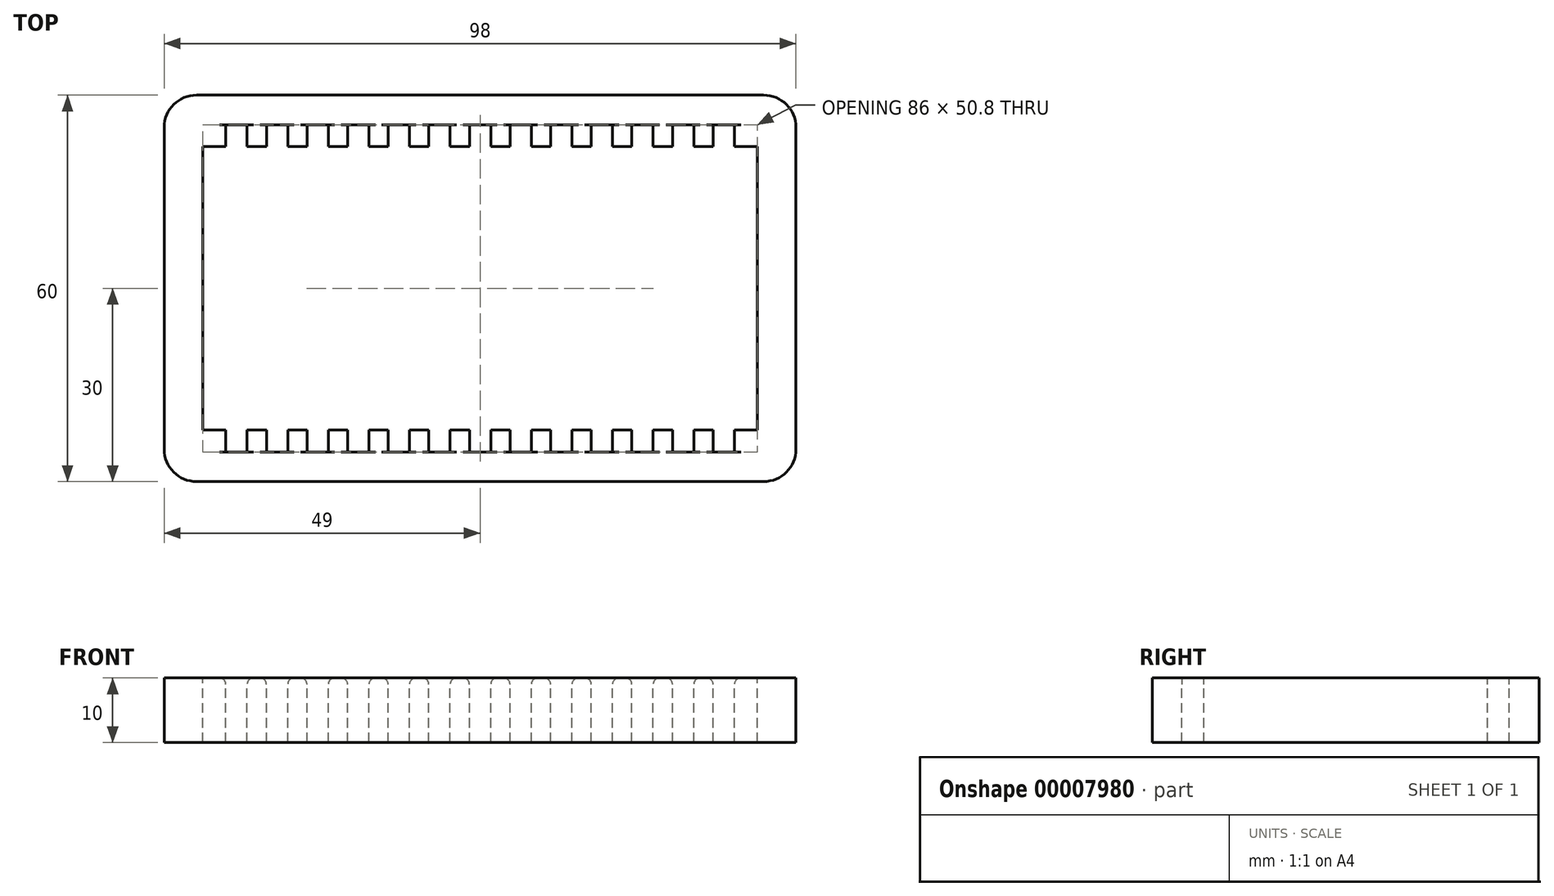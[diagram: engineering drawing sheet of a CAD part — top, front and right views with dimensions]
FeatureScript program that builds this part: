
annotation { "Feature Type Name" : "Feature", "Feature Type Description" : "" }
export const myFeature = defineFeature(function(context is Context, id is Id, definition is map)
    precondition{}
    {
        {
            var Q0;
            Q0=qCreatedBy(makeId("Top.planeOp"),FACE);
            var sketch = newSketch(context, id + "F0", { "sketchPlane" : qUnion([Q0])});
            skLineSegment(sketch, "E0.bottom", {"start": v(46, 3) * mm, "end": v(-46, 3) * mm});
            skLineSegment(sketch, "E0.top", {"start": v(49, -3) * mm, "end": v(-49, -3) * mm});
            skLineSegment(sketch, "E0.left", {"start": v(49, 0) * mm, "end": v(49, -3) * mm});
            skLineSegment(sketch, "E0.right", {"start": v(-49, 0) * mm, "end": v(-49, -3) * mm});
            skPoint(sketch, "E0.middle", {"position": v(0, 0) * mm});
            skLineSegment(sketch, "E1.bottom", {"start": v(-45.75, -3) * mm, "end": v(-42.45, -3) * mm});
            skLineSegment(sketch, "E1.top", {"start": v(-45.75, 0) * mm, "end": v(-42.45, 0) * mm});
            skLineSegment(sketch, "E1.left", {"start": v(-45.75, -3) * mm, "end": v(-45.75, 0) * mm});
            skLineSegment(sketch, "E1.right", {"start": v(-42.45, -3) * mm, "end": v(-42.45, 0) * mm});
            skLineSegment(sketch, "E2.1.0.0", {"start": v(-36.15, -3) * mm, "end": v(-36.15, 0) * mm});
            skLineSegment(sketch, "E2.1.0.1", {"start": v(-39.45, 0) * mm, "end": v(-36.15, 0) * mm});
            skLineSegment(sketch, "E2.1.0.2", {"start": v(-39.45, -3) * mm, "end": v(-39.45, 0) * mm});
            skLineSegment(sketch, "E2.2.0.0", {"start": v(-29.85, -3) * mm, "end": v(-29.85, 0) * mm});
            skLineSegment(sketch, "E2.2.0.1", {"start": v(-33.15, 0) * mm, "end": v(-29.85, 0) * mm});
            skLineSegment(sketch, "E2.2.0.2", {"start": v(-33.15, -3) * mm, "end": v(-33.15, 0) * mm});
            skLineSegment(sketch, "E2.3.0.0", {"start": v(-23.55, -3) * mm, "end": v(-23.55, 0) * mm});
            skLineSegment(sketch, "E2.3.0.1", {"start": v(-26.85, 0) * mm, "end": v(-23.55, 0) * mm});
            skLineSegment(sketch, "E2.3.0.2", {"start": v(-26.85, -3) * mm, "end": v(-26.85, 0) * mm});
            skLineSegment(sketch, "E2.4.0.0", {"start": v(-17.25, -3) * mm, "end": v(-17.25, 0) * mm});
            skLineSegment(sketch, "E2.4.0.1", {"start": v(-20.55, 0) * mm, "end": v(-17.25, 0) * mm});
            skLineSegment(sketch, "E2.4.0.2", {"start": v(-20.55, -3) * mm, "end": v(-20.55, 0) * mm});
            skLineSegment(sketch, "E2.5.0.0", {"start": v(-10.95, -3) * mm, "end": v(-10.95, 0) * mm});
            skLineSegment(sketch, "E2.5.0.1", {"start": v(-14.25, 0) * mm, "end": v(-10.95, 0) * mm});
            skLineSegment(sketch, "E2.5.0.2", {"start": v(-14.25, -3) * mm, "end": v(-14.25, 0) * mm});
            skLineSegment(sketch, "E2.6.0.0", {"start": v(-4.65, -3) * mm, "end": v(-4.65, 0) * mm});
            skLineSegment(sketch, "E2.6.0.1", {"start": v(-7.95, 0) * mm, "end": v(-4.65, 0) * mm});
            skLineSegment(sketch, "E2.6.0.2", {"start": v(-7.95, -3) * mm, "end": v(-7.95, 0) * mm});
            skLineSegment(sketch, "E2.7.0.0", {"start": v(1.65, -3) * mm, "end": v(1.65, 0) * mm});
            skLineSegment(sketch, "E2.7.0.1", {"start": v(-1.65, 0) * mm, "end": v(1.65, 0) * mm});
            skLineSegment(sketch, "E2.7.0.2", {"start": v(-1.65, -3) * mm, "end": v(-1.65, 0) * mm});
            skLineSegment(sketch, "E2.8.0.0", {"start": v(7.95, -3) * mm, "end": v(7.95, 0) * mm});
            skLineSegment(sketch, "E2.8.0.1", {"start": v(4.65, 0) * mm, "end": v(7.95, 0) * mm});
            skLineSegment(sketch, "E2.8.0.2", {"start": v(4.65, -3) * mm, "end": v(4.65, 0) * mm});
            skLineSegment(sketch, "E2.9.0.0", {"start": v(14.25, -3) * mm, "end": v(14.25, 0) * mm});
            skLineSegment(sketch, "E2.9.0.1", {"start": v(10.95, 0) * mm, "end": v(14.25, 0) * mm});
            skLineSegment(sketch, "E2.9.0.2", {"start": v(10.95, -3) * mm, "end": v(10.95, 0) * mm});
            skLineSegment(sketch, "E2.10.0.0", {"start": v(20.55, -3) * mm, "end": v(20.55, 0) * mm});
            skLineSegment(sketch, "E2.10.0.1", {"start": v(17.25, 0) * mm, "end": v(20.55, 0) * mm});
            skLineSegment(sketch, "E2.10.0.2", {"start": v(17.25, -3) * mm, "end": v(17.25, 0) * mm});
            skLineSegment(sketch, "E2.11.0.0", {"start": v(26.85, -3) * mm, "end": v(26.85, 0) * mm});
            skLineSegment(sketch, "E2.11.0.1", {"start": v(23.55, 0) * mm, "end": v(26.85, 0) * mm});
            skLineSegment(sketch, "E2.11.0.2", {"start": v(23.55, -3) * mm, "end": v(23.55, 0) * mm});
            skLineSegment(sketch, "E2.12.0.0", {"start": v(33.15, -3) * mm, "end": v(33.15, 0) * mm});
            skLineSegment(sketch, "E2.12.0.1", {"start": v(29.85, 0) * mm, "end": v(33.15, 0) * mm});
            skLineSegment(sketch, "E2.12.0.2", {"start": v(29.85, -3) * mm, "end": v(29.85, 0) * mm});
            skLineSegment(sketch, "E2.13.0.0", {"start": v(39.45, -3) * mm, "end": v(39.45, 0) * mm});
            skLineSegment(sketch, "E2.13.0.1", {"start": v(36.15, 0) * mm, "end": v(39.45, 0) * mm});
            skLineSegment(sketch, "E2.13.0.2", {"start": v(36.15, -3) * mm, "end": v(36.15, 0) * mm});
            skLineSegment(sketch, "E2.14.0.0", {"start": v(45.75, -3) * mm, "end": v(45.75, 0) * mm});
            skLineSegment(sketch, "E2.14.0.1", {"start": v(42.45, 0) * mm, "end": v(45.75, 0) * mm});
            skLineSegment(sketch, "E2.14.0.2", {"start": v(42.45, -3) * mm, "end": v(42.45, 0) * mm});
            skLineSegment(sketch, "E2.direction1", {"start": v(-42.45, -3) * mm, "end": v(-36.15, -3) * mm, "construction": true});
            skPoint(sketch, "E3.visualSharp", {"position": v(-49, 3) * mm});
            skArc(sketch, "E3.filletArc", {"start": v(-46, 3) * mm, "mid": v(-48.12, 2.12) * mm, "end": v(-49, 0) * mm});
            skPoint(sketch, "E4.visualSharp", {"position": v(49, 3) * mm});
            skArc(sketch, "E4.filletArc", {"start": v(49, 0) * mm, "mid": v(48.12, 2.12) * mm, "end": v(46, 3) * mm});
            skSolve(sketch);
        }
        {
            var Q0;
            Q0=qCreatedBy(makeId("Top.planeOp"),FACE);
            var sketch = newSketch(context, id + "F1", { "sketchPlane" : qUnion([Q0])});
            skLineSegment(sketch, "E5.bottom", {"start": v(44, -30) * mm, "end": v(-44, -30) * mm});
            skLineSegment(sketch, "E5.top", {"start": v(44, 30) * mm, "end": v(-44, 30) * mm});
            skLineSegment(sketch, "E5.left", {"start": v(49, -25) * mm, "end": v(49, 25) * mm});
            skLineSegment(sketch, "E5.right", {"start": v(-49, -25) * mm, "end": v(-49, 25) * mm});
            skPoint(sketch, "E5.middle", {"position": v(0, 0) * mm});
            skLineSegment(sketch, "E6.bottom", {"start": v(43, -22) * mm, "end": v(-43, -22) * mm});
            skLineSegment(sketch, "E6.top", {"start": v(43, 22) * mm, "end": v(-43, 22) * mm});
            skLineSegment(sketch, "E6.left", {"start": v(43, -22) * mm, "end": v(43, 22) * mm});
            skLineSegment(sketch, "E6.right", {"start": v(-43, -22) * mm, "end": v(-43, 22) * mm});
            skPoint(sketch, "E7.visualSharp", {"position": v(-49, 30) * mm});
            skArc(sketch, "E7.filletArc", {"start": v(-44, 30) * mm, "mid": v(-47.54, 28.54) * mm, "end": v(-49, 25) * mm});
            skPoint(sketch, "E8.visualSharp", {"position": v(49, 30) * mm});
            skArc(sketch, "E8.filletArc", {"start": v(49, 25) * mm, "mid": v(47.54, 28.54) * mm, "end": v(44, 30) * mm});
            skPoint(sketch, "E9.visualSharp", {"position": v(49, -30) * mm});
            skArc(sketch, "E9.filletArc", {"start": v(44, -30) * mm, "mid": v(47.54, -28.54) * mm, "end": v(49, -25) * mm});
            skPoint(sketch, "E10.visualSharp", {"position": v(-49, -30) * mm});
            skArc(sketch, "E10.filletArc", {"start": v(-49, -25) * mm, "mid": v(-47.54, -28.54) * mm, "end": v(-44, -30) * mm});
            skLineSegment(sketch, "E11.bottom", {"start": v(-1.65, 25.4) * mm, "end": v(1.65, 25.4) * mm});
            skLineSegment(sketch, "E11.top", {"start": v(-1.65, -25.4) * mm, "end": v(1.65, -25.4) * mm});
            skLineSegment(sketch, "E11.left", {"start": v(-1.65, 25.4) * mm, "end": v(-1.65, -25.4) * mm});
            skLineSegment(sketch, "E11.right", {"start": v(1.65, 25.4) * mm, "end": v(1.65, -25.4) * mm});
            skLineSegment(sketch, "E12", {"start": v(0, 25.4) * mm, "end": v(0, -25.4) * mm, "construction": true});
            skLineSegment(sketch, "E13.1.0.0", {"start": v(4.65, 25.4) * mm, "end": v(7.95, 25.4) * mm});
            skLineSegment(sketch, "E13.1.0.1", {"start": v(4.65, 25.4) * mm, "end": v(4.65, -25.4) * mm});
            skLineSegment(sketch, "E13.1.0.2", {"start": v(7.95, 25.4) * mm, "end": v(7.95, -25.4) * mm});
            skLineSegment(sketch, "E13.1.0.3", {"start": v(4.65, -25.4) * mm, "end": v(7.95, -25.4) * mm});
            skLineSegment(sketch, "E13.2.0.0", {"start": v(10.95, 25.4) * mm, "end": v(14.25, 25.4) * mm});
            skLineSegment(sketch, "E13.2.0.1", {"start": v(10.95, 25.4) * mm, "end": v(10.95, -25.4) * mm});
            skLineSegment(sketch, "E13.2.0.2", {"start": v(14.25, 25.4) * mm, "end": v(14.25, -25.4) * mm});
            skLineSegment(sketch, "E13.2.0.3", {"start": v(10.95, -25.4) * mm, "end": v(14.25, -25.4) * mm});
            skLineSegment(sketch, "E13.3.0.0", {"start": v(17.25, 25.4) * mm, "end": v(20.55, 25.4) * mm});
            skLineSegment(sketch, "E13.3.0.1", {"start": v(17.25, 25.4) * mm, "end": v(17.25, -25.4) * mm});
            skLineSegment(sketch, "E13.3.0.2", {"start": v(20.55, 25.4) * mm, "end": v(20.55, -25.4) * mm});
            skLineSegment(sketch, "E13.3.0.3", {"start": v(17.25, -25.4) * mm, "end": v(20.55, -25.4) * mm});
            skLineSegment(sketch, "E13.4.0.0", {"start": v(23.55, 25.4) * mm, "end": v(26.85, 25.4) * mm});
            skLineSegment(sketch, "E13.4.0.1", {"start": v(23.55, 25.4) * mm, "end": v(23.55, -25.4) * mm});
            skLineSegment(sketch, "E13.4.0.2", {"start": v(26.85, 25.4) * mm, "end": v(26.85, -25.4) * mm});
            skLineSegment(sketch, "E13.4.0.3", {"start": v(23.55, -25.4) * mm, "end": v(26.85, -25.4) * mm});
            skLineSegment(sketch, "E13.5.0.0", {"start": v(29.85, 25.4) * mm, "end": v(33.15, 25.4) * mm});
            skLineSegment(sketch, "E13.5.0.1", {"start": v(29.85, 25.4) * mm, "end": v(29.85, -25.4) * mm});
            skLineSegment(sketch, "E13.5.0.2", {"start": v(33.15, 25.4) * mm, "end": v(33.15, -25.4) * mm});
            skLineSegment(sketch, "E13.5.0.3", {"start": v(29.85, -25.4) * mm, "end": v(33.15, -25.4) * mm});
            skLineSegment(sketch, "E13.6.0.0", {"start": v(36.15, 25.4) * mm, "end": v(39.45, 25.4) * mm});
            skLineSegment(sketch, "E13.6.0.1", {"start": v(36.15, 25.4) * mm, "end": v(36.15, -25.4) * mm});
            skLineSegment(sketch, "E13.6.0.2", {"start": v(39.45, 25.4) * mm, "end": v(39.45, -25.4) * mm});
            skLineSegment(sketch, "E13.6.0.3", {"start": v(36.15, -25.4) * mm, "end": v(39.45, -25.4) * mm});
            skLineSegment(sketch, "E13.direction1", {"start": v(-1.65, 25.4) * mm, "end": v(4.65, 25.4) * mm, "construction": true});
            skLineSegment(sketch, "E14.MirrorCS", {"start": v(-4.65, 25.4) * mm, "end": v(-4.65, -25.4) * mm});
            skLineSegment(sketch, "E15.MirrorCS", {"start": v(-7.95, 25.4) * mm, "end": v(-7.95, -25.4) * mm});
            skLineSegment(sketch, "E16.MirrorCS", {"start": v(-10.95, 25.4) * mm, "end": v(-10.95, -25.4) * mm});
            skLineSegment(sketch, "E17.MirrorCS", {"start": v(-14.25, 25.4) * mm, "end": v(-14.25, -25.4) * mm});
            skLineSegment(sketch, "E18.MirrorCS", {"start": v(-17.25, 25.4) * mm, "end": v(-17.25, -25.4) * mm});
            skLineSegment(sketch, "E19.MirrorCS", {"start": v(-20.55, 25.4) * mm, "end": v(-20.55, -25.4) * mm});
            skLineSegment(sketch, "E20.MirrorCS", {"start": v(-23.55, 25.4) * mm, "end": v(-23.55, -25.4) * mm});
            skLineSegment(sketch, "E21.MirrorCS", {"start": v(-26.85, 25.4) * mm, "end": v(-26.85, -25.4) * mm});
            skLineSegment(sketch, "E22.MirrorCS", {"start": v(-29.85, 25.4) * mm, "end": v(-29.85, -25.4) * mm});
            skLineSegment(sketch, "E23.MirrorCS", {"start": v(-33.15, 25.4) * mm, "end": v(-33.15, -25.4) * mm});
            skLineSegment(sketch, "E24.MirrorCS", {"start": v(-36.15, 25.4) * mm, "end": v(-36.15, -25.4) * mm});
            skLineSegment(sketch, "E25.MirrorCS", {"start": v(-39.45, 25.4) * mm, "end": v(-39.45, -25.4) * mm});
            skLineSegment(sketch, "E26.MirrorCS", {"start": v(-4.65, 25.4) * mm, "end": v(-7.95, 25.4) * mm});
            skLineSegment(sketch, "E27.MirrorCS", {"start": v(-10.95, 25.4) * mm, "end": v(-14.25, 25.4) * mm});
            skLineSegment(sketch, "E28.MirrorCS", {"start": v(-17.25, 25.4) * mm, "end": v(-20.55, 25.4) * mm});
            skLineSegment(sketch, "E29.MirrorCS", {"start": v(-23.55, 25.4) * mm, "end": v(-26.85, 25.4) * mm});
            skLineSegment(sketch, "E30.MirrorCS", {"start": v(-29.85, 25.4) * mm, "end": v(-33.15, 25.4) * mm});
            skLineSegment(sketch, "E31.MirrorCS", {"start": v(-36.15, 25.4) * mm, "end": v(-39.45, 25.4) * mm});
            skLineSegment(sketch, "E32.MirrorCS", {"start": v(-4.65, -25.4) * mm, "end": v(-7.95, -25.4) * mm});
            skLineSegment(sketch, "E33.MirrorCS", {"start": v(-10.95, -25.4) * mm, "end": v(-14.25, -25.4) * mm});
            skLineSegment(sketch, "E34.MirrorCS", {"start": v(-17.25, -25.4) * mm, "end": v(-20.55, -25.4) * mm});
            skLineSegment(sketch, "E35.MirrorCS", {"start": v(-23.55, -25.4) * mm, "end": v(-26.85, -25.4) * mm});
            skLineSegment(sketch, "E36.MirrorCS", {"start": v(-29.85, -25.4) * mm, "end": v(-33.15, -25.4) * mm});
            skLineSegment(sketch, "E37.MirrorCS", {"start": v(-36.15, -25.4) * mm, "end": v(-39.45, -25.4) * mm});
            skLineSegment(sketch, "E38", {"start": v(0, 0) * mm, "end": v(-74.09, 0) * mm, "construction": true});
            skSolve(sketch);
        }
        {
            var Q0;
            Q0=makeQuery(id+"F1.imprint","IMPRINT",FACE,{"disambiguationData":[TD([[makeQuery(id+"F1.imprint","IMPRINT",EDGE,{"derivedFrom":sQuery(id+"F1.wireOp",EDGE,"E5.bottom")}),-1.0]])]});
            extrude(context, id + "F2", {"entities" : qUnion([Q0]), "oppositeDirection" : true, "depth" : 10 * mm, "offsetDistance" : 25 * mm});
        }
        {
            var Q0;
            {var subQ0=sQuery(id+"F1.wireOp",EDGE,"E24.MirrorCS");Q0=makeQuery(id+"F2.opExtrude","CAP_EDGE",EDGE,{"disambiguationData":[OSD([subQ0]),TDD([makeQuery(id+"F1.imprint","IMPRINT",EDGE,{"disambiguationData":[TD([[makeQuery(id+"F1.imprint","INTERSECT",VERTEX,{"derivedFrom":[subQ0,sQuery(id+"F1.wireOp",EDGE,"E31.MirrorCS")]}),-1.0]])],"derivedFrom":subQ0})])],"isStart":true});}
            var Q1;
            {var subQ0=sQuery(id+"F1.wireOp",EDGE,"E25.MirrorCS");Q1=makeQuery(id+"F2.opExtrude","CAP_EDGE",EDGE,{"disambiguationData":[OSD([subQ0]),TDD([makeQuery(id+"F1.imprint","IMPRINT",EDGE,{"disambiguationData":[TD([[makeQuery(id+"F1.imprint","INTERSECT",VERTEX,{"derivedFrom":[subQ0,sQuery(id+"F1.wireOp",EDGE,"E31.MirrorCS")]}),-1.0]])],"derivedFrom":subQ0})])],"isStart":true});}
            var Q2;
            {var subQ0=sQuery(id+"F1.wireOp",EDGE,"E22.MirrorCS");Q2=makeQuery(id+"F2.opExtrude","CAP_EDGE",EDGE,{"disambiguationData":[OSD([subQ0]),TDD([makeQuery(id+"F1.imprint","IMPRINT",EDGE,{"disambiguationData":[TD([[makeQuery(id+"F1.imprint","INTERSECT",VERTEX,{"derivedFrom":[subQ0,sQuery(id+"F1.wireOp",EDGE,"E30.MirrorCS")]}),-1.0]])],"derivedFrom":subQ0})])],"isStart":true});}
            var Q3;
            {var subQ0=sQuery(id+"F1.wireOp",EDGE,"E23.MirrorCS");Q3=makeQuery(id+"F2.opExtrude","CAP_EDGE",EDGE,{"disambiguationData":[OSD([subQ0]),TDD([makeQuery(id+"F1.imprint","IMPRINT",EDGE,{"disambiguationData":[TD([[makeQuery(id+"F1.imprint","INTERSECT",VERTEX,{"derivedFrom":[subQ0,sQuery(id+"F1.wireOp",EDGE,"E30.MirrorCS")]}),-1.0]])],"derivedFrom":subQ0})])],"isStart":true});}
            var Q4;
            {var subQ0=sQuery(id+"F1.wireOp",EDGE,"E21.MirrorCS");Q4=makeQuery(id+"F2.opExtrude","CAP_EDGE",EDGE,{"disambiguationData":[OSD([subQ0]),TDD([makeQuery(id+"F1.imprint","IMPRINT",EDGE,{"disambiguationData":[TD([[makeQuery(id+"F1.imprint","INTERSECT",VERTEX,{"derivedFrom":[subQ0,sQuery(id+"F1.wireOp",EDGE,"E29.MirrorCS")]}),-1.0]])],"derivedFrom":subQ0})])],"isStart":true});}
            var Q5;
            {var subQ0=sQuery(id+"F1.wireOp",EDGE,"E20.MirrorCS");Q5=makeQuery(id+"F2.opExtrude","CAP_EDGE",EDGE,{"disambiguationData":[OSD([subQ0]),TDD([makeQuery(id+"F1.imprint","IMPRINT",EDGE,{"disambiguationData":[TD([[makeQuery(id+"F1.imprint","INTERSECT",VERTEX,{"derivedFrom":[subQ0,sQuery(id+"F1.wireOp",EDGE,"E29.MirrorCS")]}),-1.0]])],"derivedFrom":subQ0})])],"isStart":true});}
            var Q6;
            {var subQ0=sQuery(id+"F1.wireOp",EDGE,"E19.MirrorCS");Q6=makeQuery(id+"F2.opExtrude","CAP_EDGE",EDGE,{"disambiguationData":[OSD([subQ0]),TDD([makeQuery(id+"F1.imprint","IMPRINT",EDGE,{"disambiguationData":[TD([[makeQuery(id+"F1.imprint","INTERSECT",VERTEX,{"derivedFrom":[subQ0,sQuery(id+"F1.wireOp",EDGE,"E28.MirrorCS")]}),-1.0]])],"derivedFrom":subQ0})])],"isStart":true});}
            var Q7;
            {var subQ0=sQuery(id+"F1.wireOp",EDGE,"E18.MirrorCS");Q7=makeQuery(id+"F2.opExtrude","CAP_EDGE",EDGE,{"disambiguationData":[OSD([subQ0]),TDD([makeQuery(id+"F1.imprint","IMPRINT",EDGE,{"disambiguationData":[TD([[makeQuery(id+"F1.imprint","INTERSECT",VERTEX,{"derivedFrom":[subQ0,sQuery(id+"F1.wireOp",EDGE,"E28.MirrorCS")]}),-1.0]])],"derivedFrom":subQ0})])],"isStart":true});}
            var Q8;
            {var subQ0=sQuery(id+"F1.wireOp",EDGE,"E17.MirrorCS");Q8=makeQuery(id+"F2.opExtrude","CAP_EDGE",EDGE,{"disambiguationData":[OSD([subQ0]),TDD([makeQuery(id+"F1.imprint","IMPRINT",EDGE,{"disambiguationData":[TD([[makeQuery(id+"F1.imprint","INTERSECT",VERTEX,{"derivedFrom":[subQ0,sQuery(id+"F1.wireOp",EDGE,"E27.MirrorCS")]}),-1.0]])],"derivedFrom":subQ0})])],"isStart":true});}
            var Q9;
            {var subQ0=sQuery(id+"F1.wireOp",EDGE,"E16.MirrorCS");Q9=makeQuery(id+"F2.opExtrude","CAP_EDGE",EDGE,{"disambiguationData":[OSD([subQ0]),TDD([makeQuery(id+"F1.imprint","IMPRINT",EDGE,{"disambiguationData":[TD([[makeQuery(id+"F1.imprint","INTERSECT",VERTEX,{"derivedFrom":[subQ0,sQuery(id+"F1.wireOp",EDGE,"E27.MirrorCS")]}),-1.0]])],"derivedFrom":subQ0})])],"isStart":true});}
            var Q10;
            {var subQ0=sQuery(id+"F1.wireOp",EDGE,"E15.MirrorCS");Q10=makeQuery(id+"F2.opExtrude","CAP_EDGE",EDGE,{"disambiguationData":[OSD([subQ0]),TDD([makeQuery(id+"F1.imprint","IMPRINT",EDGE,{"disambiguationData":[TD([[makeQuery(id+"F1.imprint","INTERSECT",VERTEX,{"derivedFrom":[subQ0,sQuery(id+"F1.wireOp",EDGE,"E26.MirrorCS")]}),-1.0]])],"derivedFrom":subQ0})])],"isStart":true});}
            var Q11;
            {var subQ0=sQuery(id+"F1.wireOp",EDGE,"E11.right");Q11=makeQuery(id+"F2.opExtrude","CAP_EDGE",EDGE,{"disambiguationData":[OSD([subQ0]),TDD([makeQuery(id+"F1.imprint","IMPRINT",EDGE,{"disambiguationData":[TD([[makeQuery(id+"F1.imprint","INTERSECT",VERTEX,{"derivedFrom":[sQuery(id+"F1.wireOp",EDGE,"E11.bottom"),subQ0]}),-1.0]])],"derivedFrom":subQ0})])],"isStart":true});}
            var Q12;
            {var subQ0=sQuery(id+"F1.wireOp",EDGE,"E11.left");Q12=makeQuery(id+"F2.opExtrude","CAP_EDGE",EDGE,{"disambiguationData":[OSD([subQ0]),TDD([makeQuery(id+"F1.imprint","IMPRINT",EDGE,{"disambiguationData":[TD([[makeQuery(id+"F1.imprint","INTERSECT",VERTEX,{"derivedFrom":[sQuery(id+"F1.wireOp",EDGE,"E11.bottom"),subQ0]}),-1.0]])],"derivedFrom":subQ0})])],"isStart":true});}
            var Q13;
            {var subQ0=sQuery(id+"F1.wireOp",EDGE,"E14.MirrorCS");Q13=makeQuery(id+"F2.opExtrude","CAP_EDGE",EDGE,{"disambiguationData":[OSD([subQ0]),TDD([makeQuery(id+"F1.imprint","IMPRINT",EDGE,{"disambiguationData":[TD([[makeQuery(id+"F1.imprint","INTERSECT",VERTEX,{"derivedFrom":[subQ0,sQuery(id+"F1.wireOp",EDGE,"E26.MirrorCS")]}),-1.0]])],"derivedFrom":subQ0})])],"isStart":true});}
            var Q14;
            {var subQ0=sQuery(id+"F1.wireOp",EDGE,"E13.1.0.2");Q14=makeQuery(id+"F2.opExtrude","CAP_EDGE",EDGE,{"disambiguationData":[OSD([subQ0]),TDD([makeQuery(id+"F1.imprint","IMPRINT",EDGE,{"disambiguationData":[TD([[makeQuery(id+"F1.imprint","INTERSECT",VERTEX,{"derivedFrom":[sQuery(id+"F1.wireOp",EDGE,"E13.1.0.0"),subQ0]}),-1.0]])],"derivedFrom":subQ0})])],"isStart":true});}
            var Q15;
            {var subQ0=sQuery(id+"F1.wireOp",EDGE,"E13.1.0.1");Q15=makeQuery(id+"F2.opExtrude","CAP_EDGE",EDGE,{"disambiguationData":[OSD([subQ0]),TDD([makeQuery(id+"F1.imprint","IMPRINT",EDGE,{"disambiguationData":[TD([[makeQuery(id+"F1.imprint","INTERSECT",VERTEX,{"derivedFrom":[sQuery(id+"F1.wireOp",EDGE,"E13.1.0.0"),subQ0]}),-1.0]])],"derivedFrom":subQ0})])],"isStart":true});}
            var Q16;
            {var subQ0=sQuery(id+"F1.wireOp",EDGE,"E13.2.0.2");Q16=makeQuery(id+"F2.opExtrude","CAP_EDGE",EDGE,{"disambiguationData":[OSD([subQ0]),TDD([makeQuery(id+"F1.imprint","IMPRINT",EDGE,{"disambiguationData":[TD([[makeQuery(id+"F1.imprint","INTERSECT",VERTEX,{"derivedFrom":[sQuery(id+"F1.wireOp",EDGE,"E13.2.0.0"),subQ0]}),-1.0]])],"derivedFrom":subQ0})])],"isStart":true});}
            var Q17;
            {var subQ0=sQuery(id+"F1.wireOp",EDGE,"E13.2.0.1");Q17=makeQuery(id+"F2.opExtrude","CAP_EDGE",EDGE,{"disambiguationData":[OSD([subQ0]),TDD([makeQuery(id+"F1.imprint","IMPRINT",EDGE,{"disambiguationData":[TD([[makeQuery(id+"F1.imprint","INTERSECT",VERTEX,{"derivedFrom":[sQuery(id+"F1.wireOp",EDGE,"E13.2.0.0"),subQ0]}),-1.0]])],"derivedFrom":subQ0})])],"isStart":true});}
            var Q18;
            {var subQ0=sQuery(id+"F1.wireOp",EDGE,"E13.3.0.2");Q18=makeQuery(id+"F2.opExtrude","CAP_EDGE",EDGE,{"disambiguationData":[OSD([subQ0]),TDD([makeQuery(id+"F1.imprint","IMPRINT",EDGE,{"disambiguationData":[TD([[makeQuery(id+"F1.imprint","INTERSECT",VERTEX,{"derivedFrom":[sQuery(id+"F1.wireOp",EDGE,"E13.3.0.0"),subQ0]}),-1.0]])],"derivedFrom":subQ0})])],"isStart":true});}
            var Q19;
            {var subQ0=sQuery(id+"F1.wireOp",EDGE,"E13.3.0.1");Q19=makeQuery(id+"F2.opExtrude","CAP_EDGE",EDGE,{"disambiguationData":[OSD([subQ0]),TDD([makeQuery(id+"F1.imprint","IMPRINT",EDGE,{"disambiguationData":[TD([[makeQuery(id+"F1.imprint","INTERSECT",VERTEX,{"derivedFrom":[sQuery(id+"F1.wireOp",EDGE,"E13.3.0.0"),subQ0]}),-1.0]])],"derivedFrom":subQ0})])],"isStart":true});}
            var Q20;
            {var subQ0=sQuery(id+"F1.wireOp",EDGE,"E13.4.0.2");Q20=makeQuery(id+"F2.opExtrude","CAP_EDGE",EDGE,{"disambiguationData":[OSD([subQ0]),TDD([makeQuery(id+"F1.imprint","IMPRINT",EDGE,{"disambiguationData":[TD([[makeQuery(id+"F1.imprint","INTERSECT",VERTEX,{"derivedFrom":[sQuery(id+"F1.wireOp",EDGE,"E13.4.0.0"),subQ0]}),-1.0]])],"derivedFrom":subQ0})])],"isStart":true});}
            var Q21;
            {var subQ0=sQuery(id+"F1.wireOp",EDGE,"E13.4.0.1");Q21=makeQuery(id+"F2.opExtrude","CAP_EDGE",EDGE,{"disambiguationData":[OSD([subQ0]),TDD([makeQuery(id+"F1.imprint","IMPRINT",EDGE,{"disambiguationData":[TD([[makeQuery(id+"F1.imprint","INTERSECT",VERTEX,{"derivedFrom":[sQuery(id+"F1.wireOp",EDGE,"E13.4.0.0"),subQ0]}),-1.0]])],"derivedFrom":subQ0})])],"isStart":true});}
            var Q22;
            {var subQ0=sQuery(id+"F1.wireOp",EDGE,"E13.5.0.2");Q22=makeQuery(id+"F2.opExtrude","CAP_EDGE",EDGE,{"disambiguationData":[OSD([subQ0]),TDD([makeQuery(id+"F1.imprint","IMPRINT",EDGE,{"disambiguationData":[TD([[makeQuery(id+"F1.imprint","INTERSECT",VERTEX,{"derivedFrom":[sQuery(id+"F1.wireOp",EDGE,"E13.5.0.0"),subQ0]}),-1.0]])],"derivedFrom":subQ0})])],"isStart":true});}
            var Q23;
            {var subQ0=sQuery(id+"F1.wireOp",EDGE,"E13.5.0.1");Q23=makeQuery(id+"F2.opExtrude","CAP_EDGE",EDGE,{"disambiguationData":[OSD([subQ0]),TDD([makeQuery(id+"F1.imprint","IMPRINT",EDGE,{"disambiguationData":[TD([[makeQuery(id+"F1.imprint","INTERSECT",VERTEX,{"derivedFrom":[sQuery(id+"F1.wireOp",EDGE,"E13.5.0.0"),subQ0]}),-1.0]])],"derivedFrom":subQ0})])],"isStart":true});}
            var Q24;
            {var subQ0=sQuery(id+"F1.wireOp",EDGE,"E13.6.0.2");Q24=makeQuery(id+"F2.opExtrude","CAP_EDGE",EDGE,{"disambiguationData":[OSD([subQ0]),TDD([makeQuery(id+"F1.imprint","IMPRINT",EDGE,{"disambiguationData":[TD([[makeQuery(id+"F1.imprint","INTERSECT",VERTEX,{"derivedFrom":[sQuery(id+"F1.wireOp",EDGE,"E13.6.0.0"),subQ0]}),-1.0]])],"derivedFrom":subQ0})])],"isStart":true});}
            var Q25;
            {var subQ0=sQuery(id+"F1.wireOp",EDGE,"E13.6.0.1");Q25=makeQuery(id+"F2.opExtrude","CAP_EDGE",EDGE,{"disambiguationData":[OSD([subQ0]),TDD([makeQuery(id+"F1.imprint","IMPRINT",EDGE,{"disambiguationData":[TD([[makeQuery(id+"F1.imprint","INTERSECT",VERTEX,{"derivedFrom":[sQuery(id+"F1.wireOp",EDGE,"E13.6.0.0"),subQ0]}),-1.0]])],"derivedFrom":subQ0})])],"isStart":true});}
            var Q26;
            {var subQ0=sQuery(id+"F1.wireOp",EDGE,"E13.6.0.1");Q26=makeQuery(id+"F2.opExtrude","CAP_EDGE",EDGE,{"disambiguationData":[OSD([subQ0]),TDD([makeQuery(id+"F1.imprint","IMPRINT",EDGE,{"disambiguationData":[TD([[makeQuery(id+"F1.imprint","INTERSECT",VERTEX,{"derivedFrom":[subQ0,sQuery(id+"F1.wireOp",EDGE,"E13.6.0.3")]}),1.0]])],"derivedFrom":subQ0})])],"isStart":true});}
            var Q27;
            {var subQ0=sQuery(id+"F1.wireOp",EDGE,"E13.6.0.2");Q27=makeQuery(id+"F2.opExtrude","CAP_EDGE",EDGE,{"disambiguationData":[OSD([subQ0]),TDD([makeQuery(id+"F1.imprint","IMPRINT",EDGE,{"disambiguationData":[TD([[makeQuery(id+"F1.imprint","INTERSECT",VERTEX,{"derivedFrom":[subQ0,sQuery(id+"F1.wireOp",EDGE,"E13.6.0.3")]}),1.0]])],"derivedFrom":subQ0})])],"isStart":true});}
            var Q28;
            {var subQ0=sQuery(id+"F1.wireOp",EDGE,"E13.5.0.2");Q28=makeQuery(id+"F2.opExtrude","CAP_EDGE",EDGE,{"disambiguationData":[OSD([subQ0]),TDD([makeQuery(id+"F1.imprint","IMPRINT",EDGE,{"disambiguationData":[TD([[makeQuery(id+"F1.imprint","INTERSECT",VERTEX,{"derivedFrom":[subQ0,sQuery(id+"F1.wireOp",EDGE,"E13.5.0.3")]}),1.0]])],"derivedFrom":subQ0})])],"isStart":true});}
            var Q29;
            {var subQ0=sQuery(id+"F1.wireOp",EDGE,"E13.5.0.1");Q29=makeQuery(id+"F2.opExtrude","CAP_EDGE",EDGE,{"disambiguationData":[OSD([subQ0]),TDD([makeQuery(id+"F1.imprint","IMPRINT",EDGE,{"disambiguationData":[TD([[makeQuery(id+"F1.imprint","INTERSECT",VERTEX,{"derivedFrom":[subQ0,sQuery(id+"F1.wireOp",EDGE,"E13.5.0.3")]}),1.0]])],"derivedFrom":subQ0})])],"isStart":true});}
            var Q30;
            {var subQ0=sQuery(id+"F1.wireOp",EDGE,"E13.4.0.2");Q30=makeQuery(id+"F2.opExtrude","CAP_EDGE",EDGE,{"disambiguationData":[OSD([subQ0]),TDD([makeQuery(id+"F1.imprint","IMPRINT",EDGE,{"disambiguationData":[TD([[makeQuery(id+"F1.imprint","INTERSECT",VERTEX,{"derivedFrom":[subQ0,sQuery(id+"F1.wireOp",EDGE,"E13.4.0.3")]}),1.0]])],"derivedFrom":subQ0})])],"isStart":true});}
            var Q31;
            {var subQ0=sQuery(id+"F1.wireOp",EDGE,"E13.4.0.1");Q31=makeQuery(id+"F2.opExtrude","CAP_EDGE",EDGE,{"disambiguationData":[OSD([subQ0]),TDD([makeQuery(id+"F1.imprint","IMPRINT",EDGE,{"disambiguationData":[TD([[makeQuery(id+"F1.imprint","INTERSECT",VERTEX,{"derivedFrom":[subQ0,sQuery(id+"F1.wireOp",EDGE,"E13.4.0.3")]}),1.0]])],"derivedFrom":subQ0})])],"isStart":true});}
            var Q32;
            {var subQ0=sQuery(id+"F1.wireOp",EDGE,"E13.3.0.2");Q32=makeQuery(id+"F2.opExtrude","CAP_EDGE",EDGE,{"disambiguationData":[OSD([subQ0]),TDD([makeQuery(id+"F1.imprint","IMPRINT",EDGE,{"disambiguationData":[TD([[makeQuery(id+"F1.imprint","INTERSECT",VERTEX,{"derivedFrom":[subQ0,sQuery(id+"F1.wireOp",EDGE,"E13.3.0.3")]}),1.0]])],"derivedFrom":subQ0})])],"isStart":true});}
            var Q33;
            {var subQ0=sQuery(id+"F1.wireOp",EDGE,"E13.3.0.1");Q33=makeQuery(id+"F2.opExtrude","CAP_EDGE",EDGE,{"disambiguationData":[OSD([subQ0]),TDD([makeQuery(id+"F1.imprint","IMPRINT",EDGE,{"disambiguationData":[TD([[makeQuery(id+"F1.imprint","INTERSECT",VERTEX,{"derivedFrom":[subQ0,sQuery(id+"F1.wireOp",EDGE,"E13.3.0.3")]}),1.0]])],"derivedFrom":subQ0})])],"isStart":true});}
            var Q34;
            {var subQ0=sQuery(id+"F1.wireOp",EDGE,"E13.2.0.2");Q34=makeQuery(id+"F2.opExtrude","CAP_EDGE",EDGE,{"disambiguationData":[OSD([subQ0]),TDD([makeQuery(id+"F1.imprint","IMPRINT",EDGE,{"disambiguationData":[TD([[makeQuery(id+"F1.imprint","INTERSECT",VERTEX,{"derivedFrom":[subQ0,sQuery(id+"F1.wireOp",EDGE,"E13.2.0.3")]}),1.0]])],"derivedFrom":subQ0})])],"isStart":true});}
            var Q35;
            {var subQ0=sQuery(id+"F1.wireOp",EDGE,"E13.2.0.1");Q35=makeQuery(id+"F2.opExtrude","CAP_EDGE",EDGE,{"disambiguationData":[OSD([subQ0]),TDD([makeQuery(id+"F1.imprint","IMPRINT",EDGE,{"disambiguationData":[TD([[makeQuery(id+"F1.imprint","INTERSECT",VERTEX,{"derivedFrom":[subQ0,sQuery(id+"F1.wireOp",EDGE,"E13.2.0.3")]}),1.0]])],"derivedFrom":subQ0})])],"isStart":true});}
            var Q36;
            {var subQ0=sQuery(id+"F1.wireOp",EDGE,"E13.1.0.1");Q36=makeQuery(id+"F2.opExtrude","CAP_EDGE",EDGE,{"disambiguationData":[OSD([subQ0]),TDD([makeQuery(id+"F1.imprint","IMPRINT",EDGE,{"disambiguationData":[TD([[makeQuery(id+"F1.imprint","INTERSECT",VERTEX,{"derivedFrom":[subQ0,sQuery(id+"F1.wireOp",EDGE,"E13.1.0.3")]}),1.0]])],"derivedFrom":subQ0})])],"isStart":true});}
            var Q37;
            {var subQ0=sQuery(id+"F1.wireOp",EDGE,"E13.1.0.2");Q37=makeQuery(id+"F2.opExtrude","CAP_EDGE",EDGE,{"disambiguationData":[OSD([subQ0]),TDD([makeQuery(id+"F1.imprint","IMPRINT",EDGE,{"disambiguationData":[TD([[makeQuery(id+"F1.imprint","INTERSECT",VERTEX,{"derivedFrom":[subQ0,sQuery(id+"F1.wireOp",EDGE,"E13.1.0.3")]}),1.0]])],"derivedFrom":subQ0})])],"isStart":true});}
            var Q38;
            {var subQ0=sQuery(id+"F1.wireOp",EDGE,"E11.right");Q38=makeQuery(id+"F2.opExtrude","CAP_EDGE",EDGE,{"disambiguationData":[OSD([subQ0]),TDD([makeQuery(id+"F1.imprint","IMPRINT",EDGE,{"disambiguationData":[TD([[makeQuery(id+"F1.imprint","INTERSECT",VERTEX,{"derivedFrom":[sQuery(id+"F1.wireOp",EDGE,"E11.top"),subQ0]}),1.0]])],"derivedFrom":subQ0})])],"isStart":true});}
            var Q39;
            {var subQ0=sQuery(id+"F1.wireOp",EDGE,"E11.left");Q39=makeQuery(id+"F2.opExtrude","CAP_EDGE",EDGE,{"disambiguationData":[OSD([subQ0]),TDD([makeQuery(id+"F1.imprint","IMPRINT",EDGE,{"disambiguationData":[TD([[makeQuery(id+"F1.imprint","INTERSECT",VERTEX,{"derivedFrom":[sQuery(id+"F1.wireOp",EDGE,"E11.top"),subQ0]}),1.0]])],"derivedFrom":subQ0})])],"isStart":true});}
            var Q40;
            {var subQ0=sQuery(id+"F1.wireOp",EDGE,"E14.MirrorCS");Q40=makeQuery(id+"F2.opExtrude","CAP_EDGE",EDGE,{"disambiguationData":[OSD([subQ0]),TDD([makeQuery(id+"F1.imprint","IMPRINT",EDGE,{"disambiguationData":[TD([[makeQuery(id+"F1.imprint","INTERSECT",VERTEX,{"derivedFrom":[subQ0,sQuery(id+"F1.wireOp",EDGE,"E32.MirrorCS")]}),1.0]])],"derivedFrom":subQ0})])],"isStart":true});}
            var Q41;
            {var subQ0=sQuery(id+"F1.wireOp",EDGE,"E15.MirrorCS");Q41=makeQuery(id+"F2.opExtrude","CAP_EDGE",EDGE,{"disambiguationData":[OSD([subQ0]),TDD([makeQuery(id+"F1.imprint","IMPRINT",EDGE,{"disambiguationData":[TD([[makeQuery(id+"F1.imprint","INTERSECT",VERTEX,{"derivedFrom":[subQ0,sQuery(id+"F1.wireOp",EDGE,"E32.MirrorCS")]}),1.0]])],"derivedFrom":subQ0})])],"isStart":true});}
            var Q42;
            {var subQ0=sQuery(id+"F1.wireOp",EDGE,"E17.MirrorCS");Q42=makeQuery(id+"F2.opExtrude","CAP_EDGE",EDGE,{"disambiguationData":[OSD([subQ0]),TDD([makeQuery(id+"F1.imprint","IMPRINT",EDGE,{"disambiguationData":[TD([[makeQuery(id+"F1.imprint","INTERSECT",VERTEX,{"derivedFrom":[subQ0,sQuery(id+"F1.wireOp",EDGE,"E33.MirrorCS")]}),1.0]])],"derivedFrom":subQ0})])],"isStart":true});}
            var Q43;
            {var subQ0=sQuery(id+"F1.wireOp",EDGE,"E16.MirrorCS");Q43=makeQuery(id+"F2.opExtrude","CAP_EDGE",EDGE,{"disambiguationData":[OSD([subQ0]),TDD([makeQuery(id+"F1.imprint","IMPRINT",EDGE,{"disambiguationData":[TD([[makeQuery(id+"F1.imprint","INTERSECT",VERTEX,{"derivedFrom":[subQ0,sQuery(id+"F1.wireOp",EDGE,"E33.MirrorCS")]}),1.0]])],"derivedFrom":subQ0})])],"isStart":true});}
            var Q44;
            {var subQ0=sQuery(id+"F1.wireOp",EDGE,"E18.MirrorCS");Q44=makeQuery(id+"F2.opExtrude","CAP_EDGE",EDGE,{"disambiguationData":[OSD([subQ0]),TDD([makeQuery(id+"F1.imprint","IMPRINT",EDGE,{"disambiguationData":[TD([[makeQuery(id+"F1.imprint","INTERSECT",VERTEX,{"derivedFrom":[subQ0,sQuery(id+"F1.wireOp",EDGE,"E34.MirrorCS")]}),1.0]])],"derivedFrom":subQ0})])],"isStart":true});}
            var Q45;
            {var subQ0=sQuery(id+"F1.wireOp",EDGE,"E19.MirrorCS");Q45=makeQuery(id+"F2.opExtrude","CAP_EDGE",EDGE,{"disambiguationData":[OSD([subQ0]),TDD([makeQuery(id+"F1.imprint","IMPRINT",EDGE,{"disambiguationData":[TD([[makeQuery(id+"F1.imprint","INTERSECT",VERTEX,{"derivedFrom":[subQ0,sQuery(id+"F1.wireOp",EDGE,"E34.MirrorCS")]}),1.0]])],"derivedFrom":subQ0})])],"isStart":true});}
            var Q46;
            {var subQ0=sQuery(id+"F1.wireOp",EDGE,"E20.MirrorCS");Q46=makeQuery(id+"F2.opExtrude","CAP_EDGE",EDGE,{"disambiguationData":[OSD([subQ0]),TDD([makeQuery(id+"F1.imprint","IMPRINT",EDGE,{"disambiguationData":[TD([[makeQuery(id+"F1.imprint","INTERSECT",VERTEX,{"derivedFrom":[subQ0,sQuery(id+"F1.wireOp",EDGE,"E35.MirrorCS")]}),1.0]])],"derivedFrom":subQ0})])],"isStart":true});}
            var Q47;
            {var subQ0=sQuery(id+"F1.wireOp",EDGE,"E21.MirrorCS");Q47=makeQuery(id+"F2.opExtrude","CAP_EDGE",EDGE,{"disambiguationData":[OSD([subQ0]),TDD([makeQuery(id+"F1.imprint","IMPRINT",EDGE,{"disambiguationData":[TD([[makeQuery(id+"F1.imprint","INTERSECT",VERTEX,{"derivedFrom":[subQ0,sQuery(id+"F1.wireOp",EDGE,"E35.MirrorCS")]}),1.0]])],"derivedFrom":subQ0})])],"isStart":true});}
            var Q48;
            {var subQ0=sQuery(id+"F1.wireOp",EDGE,"E22.MirrorCS");Q48=makeQuery(id+"F2.opExtrude","CAP_EDGE",EDGE,{"disambiguationData":[OSD([subQ0]),TDD([makeQuery(id+"F1.imprint","IMPRINT",EDGE,{"disambiguationData":[TD([[makeQuery(id+"F1.imprint","INTERSECT",VERTEX,{"derivedFrom":[subQ0,sQuery(id+"F1.wireOp",EDGE,"E36.MirrorCS")]}),1.0]])],"derivedFrom":subQ0})])],"isStart":true});}
            var Q49;
            {var subQ0=sQuery(id+"F1.wireOp",EDGE,"E23.MirrorCS");Q49=makeQuery(id+"F2.opExtrude","CAP_EDGE",EDGE,{"disambiguationData":[OSD([subQ0]),TDD([makeQuery(id+"F1.imprint","IMPRINT",EDGE,{"disambiguationData":[TD([[makeQuery(id+"F1.imprint","INTERSECT",VERTEX,{"derivedFrom":[subQ0,sQuery(id+"F1.wireOp",EDGE,"E36.MirrorCS")]}),1.0]])],"derivedFrom":subQ0})])],"isStart":true});}
            var Q50;
            {var subQ0=sQuery(id+"F1.wireOp",EDGE,"E24.MirrorCS");Q50=makeQuery(id+"F2.opExtrude","CAP_EDGE",EDGE,{"disambiguationData":[OSD([subQ0]),TDD([makeQuery(id+"F1.imprint","IMPRINT",EDGE,{"disambiguationData":[TD([[makeQuery(id+"F1.imprint","INTERSECT",VERTEX,{"derivedFrom":[subQ0,sQuery(id+"F1.wireOp",EDGE,"E37.MirrorCS")]}),1.0]])],"derivedFrom":subQ0})])],"isStart":true});}
            var Q51;
            {var subQ0=sQuery(id+"F1.wireOp",EDGE,"E25.MirrorCS");Q51=makeQuery(id+"F2.opExtrude","CAP_EDGE",EDGE,{"disambiguationData":[OSD([subQ0]),TDD([makeQuery(id+"F1.imprint","IMPRINT",EDGE,{"disambiguationData":[TD([[makeQuery(id+"F1.imprint","INTERSECT",VERTEX,{"derivedFrom":[subQ0,sQuery(id+"F1.wireOp",EDGE,"E37.MirrorCS")]}),1.0]])],"derivedFrom":subQ0})])],"isStart":true});}
            fillet(context, id + "F3", {"entities" : qUnion([Q0, Q1, Q2, Q3, Q4, Q5, Q6, Q7, Q8, Q9, Q10, Q11, Q12, Q13, Q14, Q15, Q16, Q17, Q18, Q19, Q20, Q21, Q22, Q23, Q24, Q25, Q26, Q27, Q28, Q29, Q30, Q31, Q32, Q33, Q34, Q35, Q36, Q37, Q38, Q39, Q40, Q41, Q42, Q43, Q44, Q45, Q46, Q47, Q48, Q49, Q50, Q51]), "radius" : 1 * mm, "tangentPropagation" : true, "allowEdgeOverflow" : false});
        }
    });
